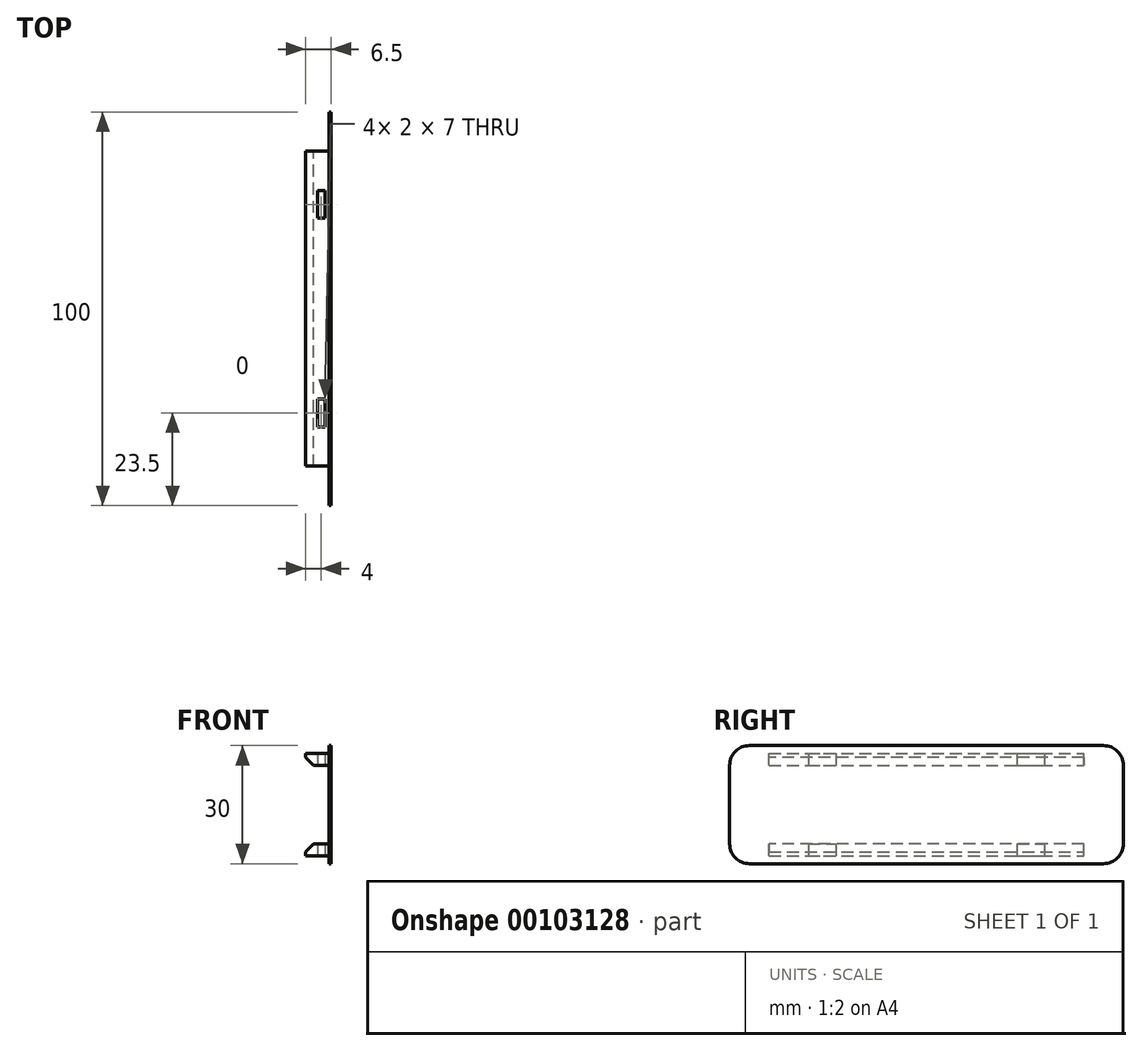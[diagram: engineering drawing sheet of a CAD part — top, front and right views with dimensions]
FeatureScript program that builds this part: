
annotation { "Feature Type Name" : "Feature", "Feature Type Description" : "" }
export const myFeature = defineFeature(function(context is Context, id is Id, definition is map)
    precondition{}
    {
        {
            var Q0;
            Q0=qCreatedBy(makeId("Right.planeOp"),FACE);
            var sketch = newSketch(context, id + "F0", { "sketchPlane" : qUnion([Q0])});
            skLineSegment(sketch, "E0.bottom", {"start": v(-45, -15) * mm, "end": v(45, -15) * mm});
            skLineSegment(sketch, "E0.top", {"start": v(-45, 15) * mm, "end": v(45, 15) * mm});
            skLineSegment(sketch, "E0.left", {"start": v(-50, -10) * mm, "end": v(-50, 10) * mm});
            skLineSegment(sketch, "E0.right", {"start": v(50, -10) * mm, "end": v(50, 10) * mm});
            skPoint(sketch, "E0.middle", {"position": v(0, 0) * mm});
            skPoint(sketch, "E1.visualSharp", {"position": v(50, 15) * mm});
            skArc(sketch, "E1.filletArc", {"start": v(50, 10) * mm, "mid": v(48.54, 13.54) * mm, "end": v(45, 15) * mm});
            skPoint(sketch, "E2.visualSharp", {"position": v(50, -15) * mm});
            skArc(sketch, "E2.filletArc", {"start": v(45, -15) * mm, "mid": v(48.54, -13.54) * mm, "end": v(50, -10) * mm});
            skPoint(sketch, "E3.visualSharp", {"position": v(-50, 15) * mm});
            skArc(sketch, "E3.filletArc", {"start": v(-45, 15) * mm, "mid": v(-48.54, 13.54) * mm, "end": v(-50, 10) * mm});
            skPoint(sketch, "E4.visualSharp", {"position": v(-50, -15) * mm});
            skArc(sketch, "E4.filletArc", {"start": v(-50, -10) * mm, "mid": v(-48.54, -13.54) * mm, "end": v(-45, -15) * mm});
            skSolve(sketch);
        }
        {
            var Q0;
            Q0=makeQuery(id+"F0.imprint","IMPRINT",FACE,{"disambiguationData":[TD([[makeQuery(id+"F0.imprint","IMPRINT",EDGE,{"derivedFrom":sQuery(id+"F0.wireOp",EDGE,"E0.bottom")}),1.0]])]});
            extrude(context, id + "F1", {"entities" : qUnion([Q0]), "depth" : 0.5 * mm, "offsetDistance" : 25 * mm});
        }
        {
            var Q0;
            Q0=makeQuery(id+"F1.opExtrude","CAP_FACE",FACE,{"disambiguationData":[OSD([sQuery(id+"F0.wireOp",EDGE,"E0.bottom"),sQuery(id+"F0.wireOp",EDGE,"E0.top"),sQuery(id+"F0.wireOp",EDGE,"E0.left"),sQuery(id+"F0.wireOp",EDGE,"E0.right"),sQuery(id+"F0.wireOp",EDGE,"E1.filletArc"),sQuery(id+"F0.wireOp",EDGE,"E2.filletArc"),sQuery(id+"F0.wireOp",EDGE,"E3.filletArc"),sQuery(id+"F0.wireOp",EDGE,"E4.filletArc")])],"isStart":true});
            var sketch = newSketch(context, id + "F2", { "sketchPlane" : qUnion([Q0])});
            skLineSegment(sketch, "E5.bottom", {"start": v(40, 13) * mm, "end": v(-40, 13) * mm});
            skLineSegment(sketch, "E5.top", {"start": v(40, 10) * mm, "end": v(-40, 10) * mm});
            skLineSegment(sketch, "E5.left", {"start": v(40, 10) * mm, "end": v(40, 13) * mm});
            skLineSegment(sketch, "E5.right", {"start": v(-40, 10) * mm, "end": v(-40, 13) * mm});
            skPoint(sketch, "E5.middle", {"position": v(0, 11.5) * mm});
            skLineSegment(sketch, "E6.bottom", {"start": v(40, -13) * mm, "end": v(-40, -13) * mm});
            skLineSegment(sketch, "E6.top", {"start": v(40, -10) * mm, "end": v(-40, -10) * mm});
            skLineSegment(sketch, "E6.left", {"start": v(40, -13) * mm, "end": v(40, -10) * mm});
            skLineSegment(sketch, "E6.right", {"start": v(-40, -13) * mm, "end": v(-40, -10) * mm});
            skPoint(sketch, "E6.middle", {"position": v(0, -11.5) * mm});
            skSolve(sketch);
        }
        {
            var Q0;
            Q0=makeQuery(id+"F2.imprint","IMPRINT",FACE,{"disambiguationData":[TD([[makeQuery(id+"F2.imprint","IMPRINT",EDGE,{"derivedFrom":sQuery(id+"F2.wireOp",EDGE,"E5.bottom")}),1.0]])]});
            var Q1;
            Q1=makeQuery(id+"F2.imprint","IMPRINT",FACE,{"disambiguationData":[TD([[makeQuery(id+"F2.imprint","IMPRINT",EDGE,{"derivedFrom":sQuery(id+"F2.wireOp",EDGE,"E6.bottom")}),-1.0]])]});
            extrude(context, id + "F3", {"entities" : qUnion([Q0, Q1]), "operationType" : NewBodyOperationType.ADD, "depth" : 6 * mm, "offsetDistance" : 25 * mm});
        }
        {
            var Q0;
            Q0=makeQuery(id+"F3.opExtrude","SWEPT_FACE",FACE,{"disambiguationData":[OSD([sQuery(id+"F2.wireOp",EDGE,"E6.bottom")])]});
            var sketch = newSketch(context, id + "F4", { "sketchPlane" : qUnion([Q0])});
            skLineSegment(sketch, "E7.bottom", {"start": v(-1, -23) * mm, "end": v(-3, -23) * mm});
            skLineSegment(sketch, "E7.top", {"start": v(-1, -30) * mm, "end": v(-3, -30) * mm});
            skLineSegment(sketch, "E7.left", {"start": v(-1, -23) * mm, "end": v(-1, -30) * mm});
            skLineSegment(sketch, "E7.right", {"start": v(-3, -23) * mm, "end": v(-3, -30) * mm});
            skPoint(sketch, "E7.middle", {"position": v(-2, -26.5) * mm});
            skLineSegment(sketch, "E8.bottom", {"start": v(-1, 30) * mm, "end": v(-3, 30) * mm});
            skLineSegment(sketch, "E8.top", {"start": v(-1, 23) * mm, "end": v(-3, 23) * mm});
            skLineSegment(sketch, "E8.left", {"start": v(-1, 30) * mm, "end": v(-1, 23) * mm});
            skLineSegment(sketch, "E8.right", {"start": v(-3, 30) * mm, "end": v(-3, 23) * mm});
            skPoint(sketch, "E8.middle", {"position": v(-2, 26.5) * mm});
            skSolve(sketch);
        }
        {
            var Q0;
            Q0=makeQuery(id+"F4.imprint","IMPRINT",FACE,{"disambiguationData":[TD([[makeQuery(id+"F4.imprint","IMPRINT",EDGE,{"derivedFrom":sQuery(id+"F4.wireOp",EDGE,"E7.bottom")}),1.0]])]});
            var Q1;
            Q1=makeQuery(id+"F4.imprint","IMPRINT",FACE,{"disambiguationData":[TD([[makeQuery(id+"F4.imprint","IMPRINT",EDGE,{"derivedFrom":sQuery(id+"F4.wireOp",EDGE,"E8.bottom")}),1.0]])]});
            extrude(context, id + "F5", {"entities" : qUnion([Q0, Q1]), "operationType" : NewBodyOperationType.REMOVE, "oppositeDirection" : true, "depth" : 80 * mm, "offsetDistance" : 25 * mm});
        }
        {
            var Q0;
            Q0=makeQuery(id+"F3.opExtrude","CAP_EDGE",EDGE,{"disambiguationData":[OSD([sQuery(id+"F2.wireOp",EDGE,"E6.top")])],"isStart":false});
            var Q1;
            Q1=makeQuery(id+"F3.opExtrude","CAP_EDGE",EDGE,{"disambiguationData":[OSD([sQuery(id+"F2.wireOp",EDGE,"E5.top")])],"isStart":false});
            chamfer(context, id + "F6", {"entities" : qUnion([Q0, Q1]), "width" : 2 * mm, "tangentPropagation" : true});
        }
    });
